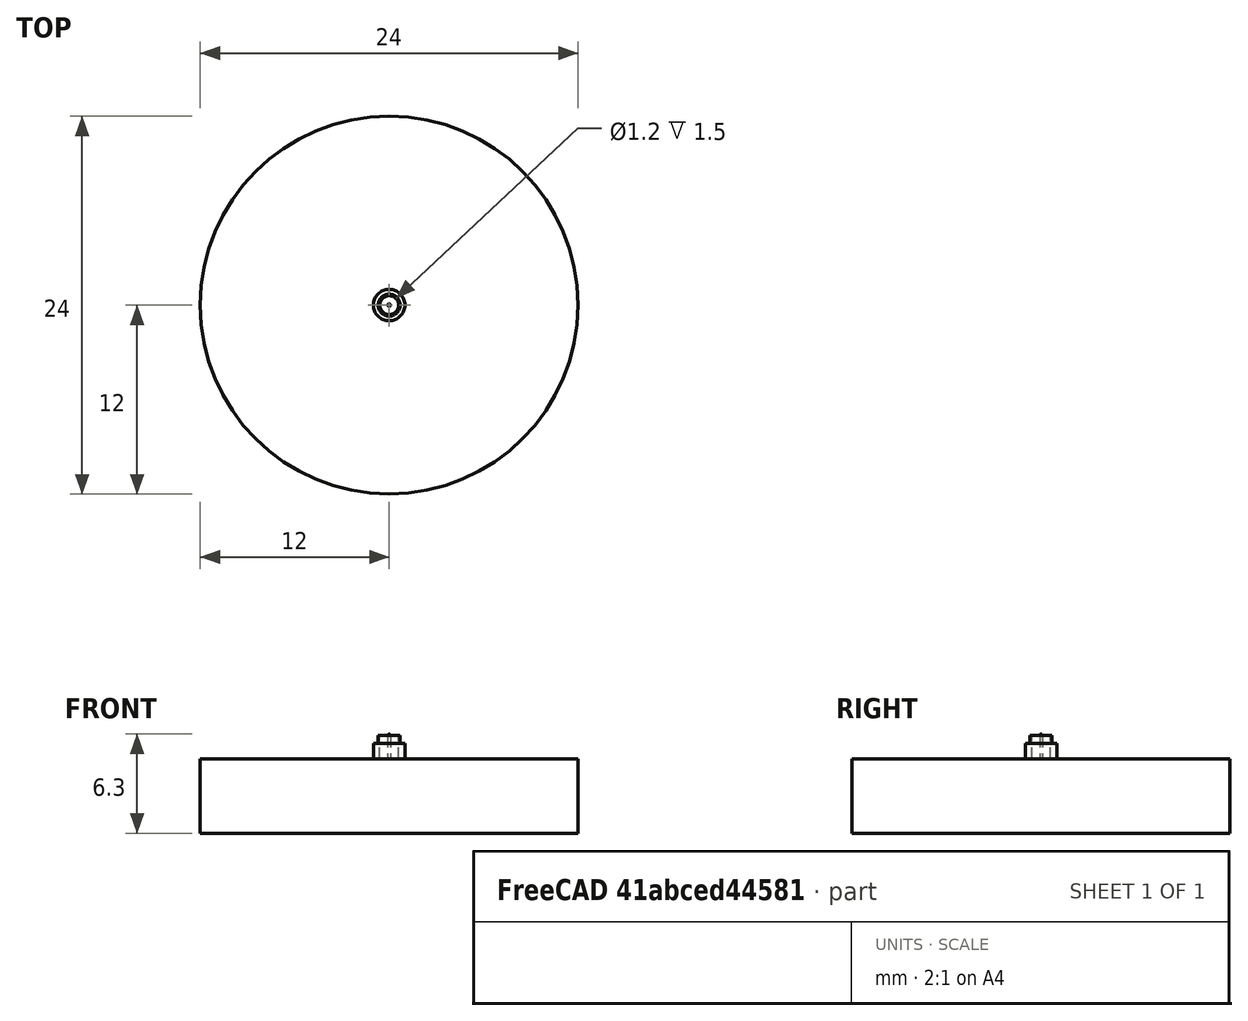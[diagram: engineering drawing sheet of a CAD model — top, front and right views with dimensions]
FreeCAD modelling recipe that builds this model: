
FCSTD DOCUMENT  (FreeCAD 0.19R20415 (Git))
Label: Vostok_Amphibia_Movement_2416B
License: All rights reserved
LicenseURL: http://en.wikipedia.org/wiki/All_rights_reserved
objects: Sketcher::SketchObject×1, PartDesign::Revolution×1, PartDesign::Body×1
note: 4 computed .brp shape members not serialized (recipe doc carries the construction recipe); baked Part::Feature solids carry a one-line shape summary decoded from their .brp

FEATURE [Sketcher::SketchObject] Sketch
  MapMode = 5
  Placement = pos=(0,0,0) rot=(1,0,0;1.5708rad)
  Support = -> [XZ_Plane]
  sketch-geometry (12):
    g0: LineSegment StartX=0.085 StartY=6.215 StartZ=0 EndX=0.085 EndY=4.715 EndZ=0
    g1: LineSegment StartX=0.085 StartY=4.715 StartZ=0 EndX=0.6 EndY=4.715 EndZ=0
    g2: LineSegment StartX=0.6 StartY=4.715 StartZ=0 EndX=0.6 EndY=6.215 EndZ=0
    g3: LineSegment StartX=0.6 StartY=6.215 StartZ=0 EndX=0.7 EndY=6.215 EndZ=0
    g4: LineSegment StartX=0.7 StartY=6.215 StartZ=0 EndX=0.7 EndY=5.715 EndZ=0
    g5: LineSegment StartX=12 StartY=4.715 StartZ=0 EndX=12 EndY=0 EndZ=0
    g6: LineSegment StartX=12 StartY=0 StartZ=0 EndX=0 EndY=0 EndZ=0
    g7: LineSegment StartX=0 StartY=0 StartZ=0 EndX=0 EndY=6.3 EndZ=0
    g8: ArcOfCircle CenterX=0 CenterY=6.215 CenterZ=0 NormalX=0 NormalY=0 NormalZ=1 AngleXU=0 Radius=0.085 StartAngle=2.8e-15 EndAngle=1.5708
    g9: LineSegment StartX=0.7 StartY=5.715 StartZ=0 EndX=1 EndY=5.715 EndZ=0
    g10: LineSegment StartX=1 StartY=5.715 StartZ=0 EndX=1 EndY=4.715 EndZ=0
    g11: LineSegment StartX=1 StartY=4.715 StartZ=0 EndX=12 EndY=4.715 EndZ=0
  constraints (36):
    c: PointOnObject(g7,g-2)
    c: Vertical(g0)
    c: Coincident(g0,g1)
    c: Horizontal(g1)
    c: Coincident(g1,g2)
    c: Vertical(g2)
    c: Coincident(g2,g3)
    c: Horizontal(g3)
    c: Coincident(g3,g4)
    c: Vertical(g4)
    c: PointOnObject(g5,g-1)
    c: Vertical(g5)
    c: Coincident(g5,g6)
    c: Coincident(g6,g-1)
    c: Coincident(g6,g7)
    c: DistanceX(g6,g6) = 12
    c: DistanceY(g4,g4) = 0.5
    c: DistanceY(g7) = 6.3
    c: PointOnObject(g8,g7)
    c: Coincident(g8,g7)
    c: Coincident(g8,g0)
    c: Horizontal(g8,g0)
    c: DistanceX(g0) = 0.085
    c: DistanceX(g3) = 0.7
    c: Coincident(g4,g9)
    c: Horizontal(g9)
    c: Coincident(g9,g10)
    c: Coincident(g10,g11)
    c: Coincident(g11,g5)
    c: Horizontal(g11)
    c: Vertical(g10)
    c: DistanceX(g3,g3) = 0.1
    c: Horizontal(g0,g2)
    c: DistanceY(g10,g10) = 1
    c: DistanceX(g9,g9) = 0.3
    c: Horizontal(g1,g10)
FEATURE [PartDesign::Revolution] Revolution
  AllowMultiFace = false
  Angle = 360
  Axis = (0,2e-16,1)
  Base = (0,0,0)
  Placement = pos=(0,0,0) rot=(1,0,0;1.5708rad)
  Profile = -> Sketch
  ReferenceAxis = -> Sketch [V_Axis]
  Reversed = true
FEATURE [PartDesign::Body] Body  label="Movement"
  Group = -> [Sketch,Revolution]
  Origin = -> Origin
  Tip = -> Revolution
